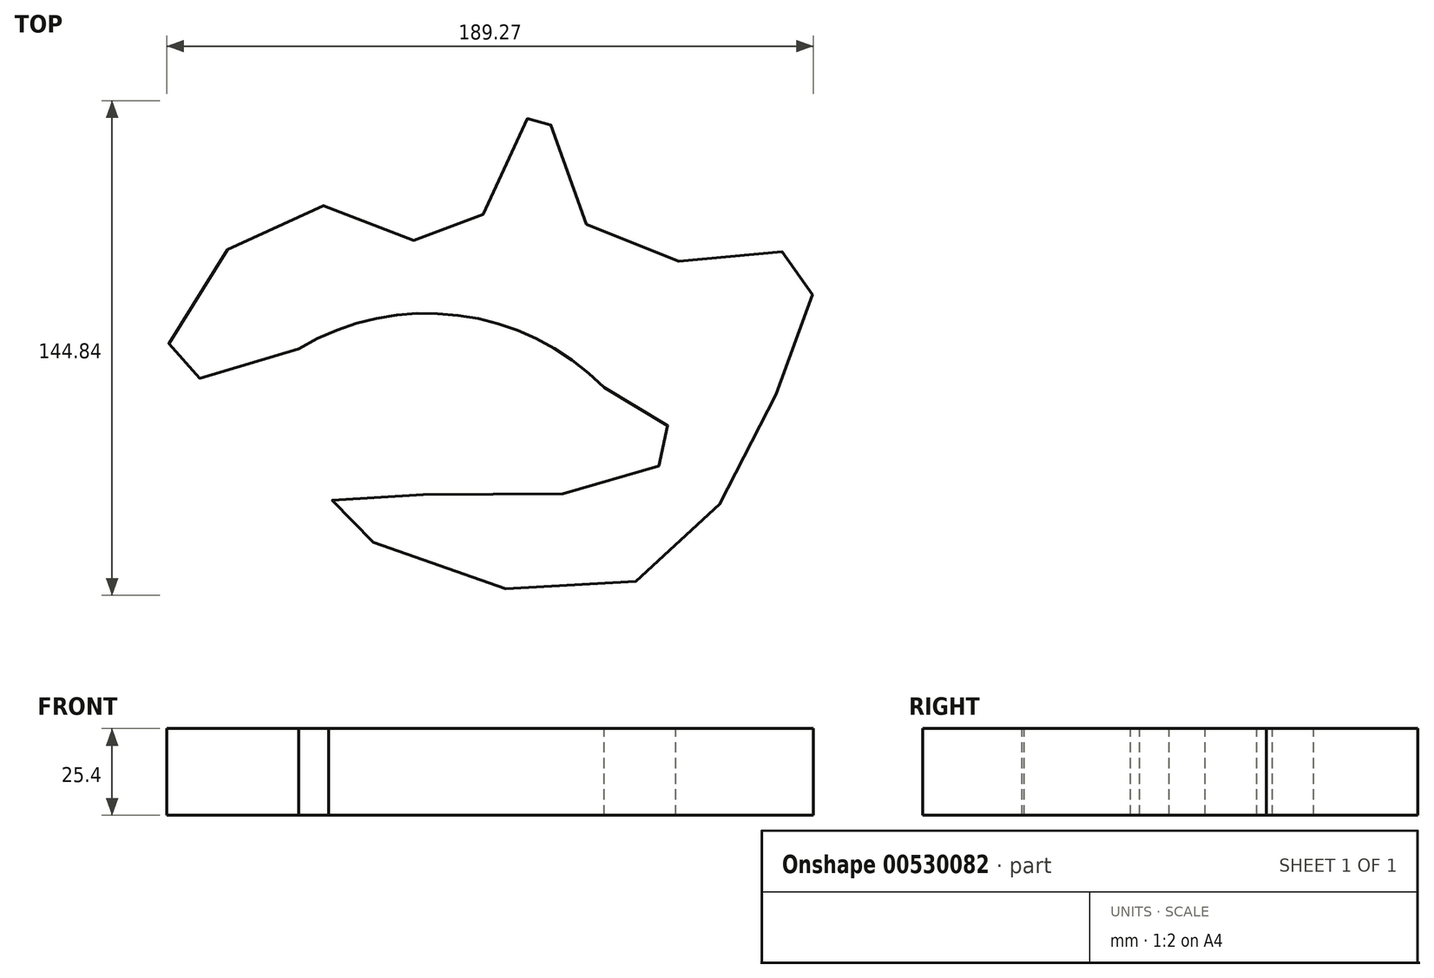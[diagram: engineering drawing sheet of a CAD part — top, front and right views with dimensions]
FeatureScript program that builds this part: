
annotation { "Feature Type Name" : "Feature", "Feature Type Description" : "" }
export const myFeature = defineFeature(function(context is Context, id is Id, definition is map)
    precondition{}
    {
        {
            var Q0;
            Q0=qCreatedBy(makeId("Top.planeOp"),FACE);
            var sketch = newSketch(context, id + "F0", { "sketchPlane" : qUnion([Q0])});
            skArc(sketch, "E0", {"start": v(0, 0) * mm, "mid": v(-42.75, 21.2) * mm, "end": v(-89.44, 11.36) * mm});
            skFitSpline(sketch, "E1", {"points": [v(-89.44, 11.36) * mm, v(-127.7, 6.4) * mm, v(-89.44, 53.2) * mm, v(-42.63, 43.02) * mm, v(-18.96, 84.04) * mm, v(0, 42.2) * mm, v(57.58, 38.61) * mm, v(49.87, -2.96) * mm, v(-4.92, -60.5) * mm, v(-80.63, -34.34) * mm, v(-9.05, -30.77) * mm, v(20.96, -15.35) * mm, v(0, 0) * mm], "startDerivative": vector(-743.63, -271) * mm, "endDerivative": vector(-514.4, 249.8) * mm});
            skSolve(sketch);
        }
        {
            var Q0;
            Q0 = qSketchRegion(id + "F0", true);
            extrude(context, id + "F1", {"entities" : qUnion([Q0]), "oppositeDirection" : true, "depth" : 25.4 * mm, "offsetDistance" : 25.4 * mm});
        }
    });
